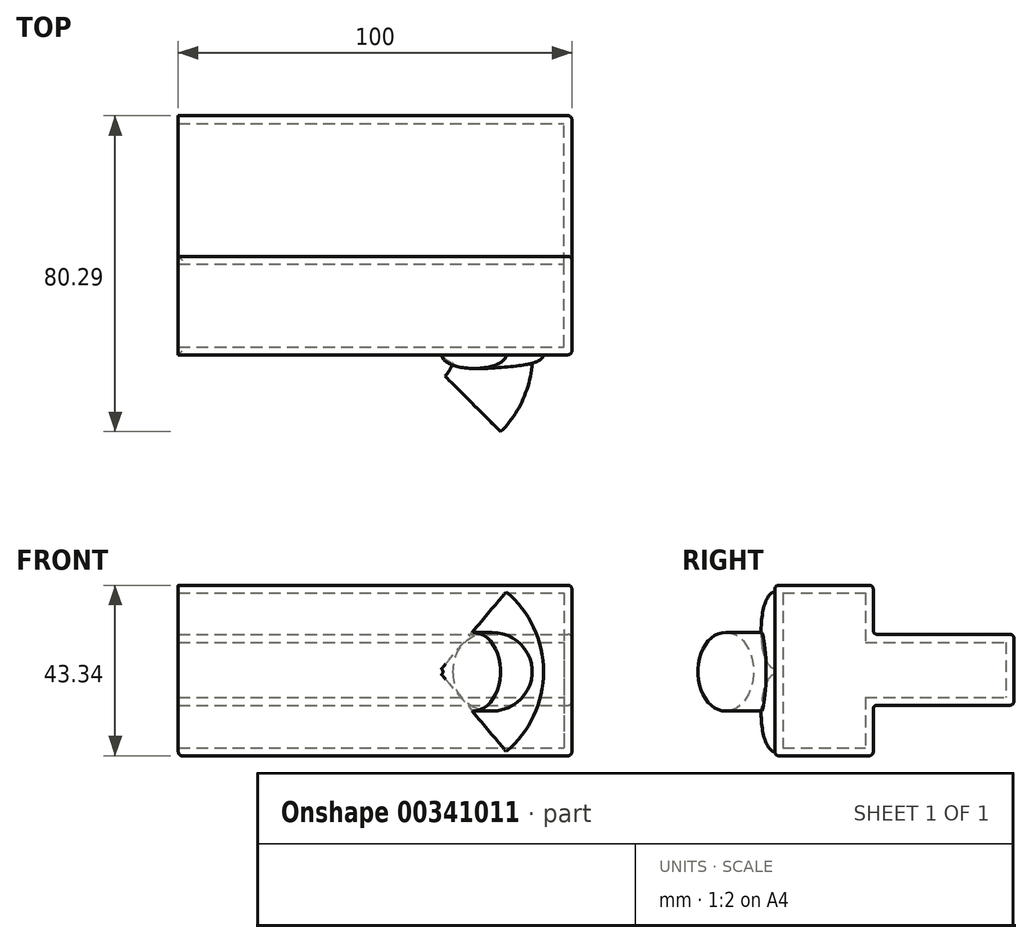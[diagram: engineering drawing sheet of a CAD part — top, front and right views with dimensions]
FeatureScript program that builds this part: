
annotation { "Feature Type Name" : "Feature", "Feature Type Description" : "" }
export const myFeature = defineFeature(function(context is Context, id is Id, definition is map)
    precondition{}
    {
        {
            var Q0;
            Q0=qCreatedBy(makeId("Front.planeOp"),FACE);
            var sketch = newSketch(context, id + "F0", { "sketchPlane" : qUnion([Q0])});
            skCircle(sketch, "E0", {"center": v(0, 0) * mm, "radius": 10 * mm});
            skSolve(sketch);
        }
        {
            var Q0;
            Q0=qCreatedBy(makeId("Front.planeOp"),FACE);
            var sketch = newSketch(context, id + "F1", { "sketchPlane" : qUnion([Q0])});
            skLineSegment(sketch, "E1", {"start": v(-17.65, 8.88) * mm, "end": v(-17.65, -11.04) * mm});
            skSolve(sketch);
        }
        {
            var Q0;
            Q0=makeQuery(id+"F0.imprint","IMPRINT",FACE,{"disambiguationData":[TD([[makeQuery(id+"F0.imprint","IMPRINT",EDGE,{"derivedFrom":sQuery(id+"F0.wireOp",EDGE,"E0")}),1.0]])]});
            var Q1;
            Q1=sQuery(id+"F1.wireOp",EDGE,"E1");
            revolve(context, id + "F2", {"entities" : qUnion([Q0]), "axis" : qUnion([Q1]), "revolveType" : RevolveType.TWO_DIRECTIONS, "angle" : 45 * degree, "angleBack" : 270 * degree});
        }
        {
            var Q0;
            Q0=qCreatedBy(makeId("Top.planeOp"),FACE);
            var sketch = newSketch(context, id + "F3", { "sketchPlane" : qUnion([Q0])});
            skEllipse(sketch, "E2", {"center": v(0, 0) * mm, "majorRadius": 12.78 * mm, "minorRadius": 3.48 * mm, "majorAxis": v(1, 0)});
            skSolve(sketch);
        }
        {
            var Q0;
            Q0=qCreatedBy(makeId("Top.planeOp"),FACE);
            var sketch = newSketch(context, id + "F4", { "sketchPlane" : qUnion([Q0])});
            skLineSegment(sketch, "E3", {"start": v(-13.72, -2.71) * mm, "end": v(-13.72, 2.44) * mm});
            skSolve(sketch);
        }
        {
            var Q0;
            Q0=makeQuery(id+"F3.imprint","IMPRINT",FACE,{"disambiguationData":[TD([[makeQuery(id+"F3.imprint","IMPRINT",EDGE,{"derivedFrom":sQuery(id+"F3.wireOp",EDGE,"E2")}),1.0]])]});
            var Q1;
            Q1=sQuery(id+"F4.wireOp",EDGE,"E3");
            revolve(context, id + "F5", {"operationType" : NewBodyOperationType.ADD, "entities" : qUnion([Q0]), "axis" : qUnion([Q1]), "revolveType" : RevolveType.SYMMETRIC, "angle" : 100 * degree});
        }
        {
            var Q0;
            Q0=qCreatedBy(makeId("Right.planeOp"),FACE);
            var sketch = newSketch(context, id + "F6", { "sketchPlane" : qUnion([Q0])});
            skLineSegment(sketch, "E4.bottom", {"start": v(0, 21.97) * mm, "end": v(25, 21.97) * mm});
            skLineSegment(sketch, "E4.top", {"start": v(0, -21.37) * mm, "end": v(25, -21.37) * mm});
            skLineSegment(sketch, "E4.left", {"start": v(0, 21.97) * mm, "end": v(0, -21.37) * mm});
            skLineSegment(sketch, "E4.right", {"start": v(25, 21.97) * mm, "end": v(25, -21.37) * mm});
            skSolve(sketch);
        }
        {
            var Q0;
            Q0=makeQuery(id+"F6.imprint","IMPRINT",FACE,{"disambiguationData":[TD([[makeQuery(id+"F6.imprint","IMPRINT",EDGE,{"derivedFrom":sQuery(id+"F6.wireOp",EDGE,"E4.bottom")}),-1.0]])]});
            extrude(context, id + "F7", {"entities" : qUnion([Q0]), "operationType" : NewBodyOperationType.ADD, "oppositeDirection" : true, "depth" : 80 * mm, "hasSecondDirection" : true, "secondDirectionOppositeDirection" : false, "secondDirectionDepth" : 20 * mm});
        }
        {
            var Q0;
            Q0=qCreatedBy(makeId("Right.planeOp"),FACE);
            var sketch = newSketch(context, id + "F8", { "sketchPlane" : qUnion([Q0])});
            skLineSegment(sketch, "E5.bottom", {"start": v(22.33, 9.48) * mm, "end": v(60.74, 9.48) * mm});
            skLineSegment(sketch, "E5.top", {"start": v(22.33, -8.52) * mm, "end": v(60.74, -8.52) * mm});
            skLineSegment(sketch, "E5.left", {"start": v(22.33, 9.48) * mm, "end": v(22.33, -8.52) * mm});
            skLineSegment(sketch, "E5.right", {"start": v(60.74, 9.48) * mm, "end": v(60.74, -8.52) * mm});
            skSolve(sketch);
        }
        {
            var Q0;
            Q0=makeQuery(id+"F8.imprint","IMPRINT",FACE,{"disambiguationData":[TD([[makeQuery(id+"F8.imprint","IMPRINT",EDGE,{"derivedFrom":sQuery(id+"F8.wireOp",EDGE,"E5.bottom")}),-1.0]])]});
            extrude(context, id + "F9", {"entities" : qUnion([Q0]), "operationType" : NewBodyOperationType.ADD, "oppositeDirection" : true, "depth" : 80 * mm, "hasSecondDirection" : true, "secondDirectionOppositeDirection" : false, "secondDirectionDepth" : 20 * mm});
        }
        {
            var Q0;
            Q0=makeQuery(id+"F9.boolean.opBoolean","MERGE",FACE,{"derivedFrom":[makeQuery(id+"F7.opExtrude","CAP_FACE",FACE,{"disambiguationData":[OSD([sQuery(id+"F6.wireOp",EDGE,"E4.bottom"),sQuery(id+"F6.wireOp",EDGE,"E4.top"),sQuery(id+"F6.wireOp",EDGE,"E4.left"),sQuery(id+"F6.wireOp",EDGE,"E4.right")])],"isStart":false}),makeQuery(id+"F9.opExtrude","CAP_FACE",FACE,{"disambiguationData":[OSD([sQuery(id+"F8.wireOp",EDGE,"E5.bottom"),sQuery(id+"F8.wireOp",EDGE,"E5.top"),sQuery(id+"F8.wireOp",EDGE,"E5.left"),sQuery(id+"F8.wireOp",EDGE,"E5.right")])],"isStart":false})]});
            shell(context, id + "F10", {"entities" : qUnion([Q0]), "thickness" : 2 * mm});
        }
        {
            var Q0;
            Q0=makeQuery(id+"F7.opExtrude","SWEPT_EDGE",EDGE,{"disambiguationData":[OSD([sQuery(id+"F6.wireOp",EDGE,"E4.top"),sQuery(id+"F6.wireOp",EDGE,"E4.left")])]});
            var Q1;
            Q1=makeQuery(id+"F7.opExtrude","CAP_EDGE",EDGE,{"disambiguationData":[OSD([sQuery(id+"F6.wireOp",EDGE,"E4.top")])],"isStart":false});
            var Q2;
            Q2=makeQuery(id+"F7.opExtrude","SWEPT_EDGE",EDGE,{"disambiguationData":[OSD([sQuery(id+"F6.wireOp",EDGE,"E4.top"),sQuery(id+"F6.wireOp",EDGE,"E4.right")])]});
            var Q3;
            Q3=makeQuery(id+"F7.opExtrude","CAP_EDGE",EDGE,{"disambiguationData":[OSD([sQuery(id+"F6.wireOp",EDGE,"E4.top")])],"isStart":true});
            var Q4;
            Q4=makeQuery(id+"F7.opExtrude","CAP_EDGE",EDGE,{"disambiguationData":[OSD([sQuery(id+"F6.wireOp",EDGE,"E4.left")])],"isStart":true});
            var Q5;
            Q5=makeQuery(id+"F7.opExtrude","SWEPT_EDGE",EDGE,{"disambiguationData":[OSD([sQuery(id+"F6.wireOp",EDGE,"E4.bottom"),sQuery(id+"F6.wireOp",EDGE,"E4.left")])]});
            var Q6;
            Q6=makeQuery(id+"F9.opExtrude","SWEPT_EDGE",EDGE,{"disambiguationData":[OSD([sQuery(id+"F8.wireOp",EDGE,"E5.bottom"),sQuery(id+"F8.wireOp",EDGE,"E5.right")])]});
            var Q7;
            Q7=makeQuery(id+"F7.opExtrude","SWEPT_EDGE",EDGE,{"disambiguationData":[OSD([sQuery(id+"F6.wireOp",EDGE,"E4.bottom"),sQuery(id+"F6.wireOp",EDGE,"E4.right")])]});
            var Q8;
            Q8=makeQuery(id+"F7.opExtrude","CAP_EDGE",EDGE,{"disambiguationData":[OSD([sQuery(id+"F6.wireOp",EDGE,"E4.bottom")])],"isStart":true});
            var Q9;
            Q9=makeQuery(id+"F9.opExtrude","CAP_EDGE",EDGE,{"disambiguationData":[OSD([sQuery(id+"F8.wireOp",EDGE,"E5.bottom")])],"isStart":true});
            var Q10;
            Q10=makeQuery(id+"F9.opExtrude","CAP_EDGE",EDGE,{"disambiguationData":[OSD([sQuery(id+"F8.wireOp",EDGE,"E5.top")])],"isStart":true});
            var Q11;
            {var subQ1=sQuery(id+"F6.wireOp",EDGE,"E4.right");var subQ2=sQuery(id+"F6.wireOp",EDGE,"E4.top");Q11=makeQuery(id+"F9.boolean.opBoolean","SPLIT",EDGE,{"disambiguationData":[TD([makeQuery(id+"F7.opExtrude","SWEPT_FACE",FACE,{"disambiguationData":[OSD([subQ2])]})])],"derivedFrom":makeQuery(id+"F7.opExtrude","CAP_EDGE",EDGE,{"disambiguationData":[OSD([subQ1])],"isStart":true})});}
            var Q12;
            {var subQ1=sQuery(id+"F6.wireOp",EDGE,"E4.right");var subQ2=sQuery(id+"F6.wireOp",EDGE,"E4.bottom");Q12=makeQuery(id+"F9.boolean.opBoolean","SPLIT",EDGE,{"disambiguationData":[TD([makeQuery(id+"F7.opExtrude","SWEPT_FACE",FACE,{"disambiguationData":[OSD([subQ2])]})])],"derivedFrom":makeQuery(id+"F7.opExtrude","CAP_EDGE",EDGE,{"disambiguationData":[OSD([subQ1])],"isStart":true})});}
            var Q13;
            Q13=makeQuery(id+"F9.opExtrude","CAP_EDGE",EDGE,{"disambiguationData":[OSD([sQuery(id+"F8.wireOp",EDGE,"E5.right")])],"isStart":true});
            var Q14;
            Q14=makeQuery(id+"F9.boolean.opBoolean","INTERSECT",EDGE,{"derivedFrom":[makeQuery(id+"F7.opExtrude","SWEPT_FACE",FACE,{"disambiguationData":[OSD([sQuery(id+"F6.wireOp",EDGE,"E4.right")])]}),makeQuery(id+"F9.opExtrude","SWEPT_FACE",FACE,{"disambiguationData":[OSD([sQuery(id+"F8.wireOp",EDGE,"E5.top")])]})]});
            var Q15;
            Q15=makeQuery(id+"F9.opExtrude","SWEPT_EDGE",EDGE,{"disambiguationData":[OSD([sQuery(id+"F8.wireOp",EDGE,"E5.top"),sQuery(id+"F8.wireOp",EDGE,"E5.right")])]});
            var Q16;
            Q16=makeQuery(id+"F9.boolean.opBoolean","INTERSECT",EDGE,{"derivedFrom":[makeQuery(id+"F7.opExtrude","SWEPT_FACE",FACE,{"disambiguationData":[OSD([sQuery(id+"F6.wireOp",EDGE,"E4.right")])]}),makeQuery(id+"F9.opExtrude","SWEPT_FACE",FACE,{"disambiguationData":[OSD([sQuery(id+"F8.wireOp",EDGE,"E5.bottom")])]})]});
            fillet(context, id + "F11", {"entities" : qUnion([Q0, Q1, Q2, Q3, Q4, Q5, Q6, Q7, Q8, Q9, Q10, Q11, Q12, Q13, Q14, Q15, Q16]), "radius" : 1 * mm, "tangentPropagation" : true, "allowEdgeOverflow" : false});
        }
    });
